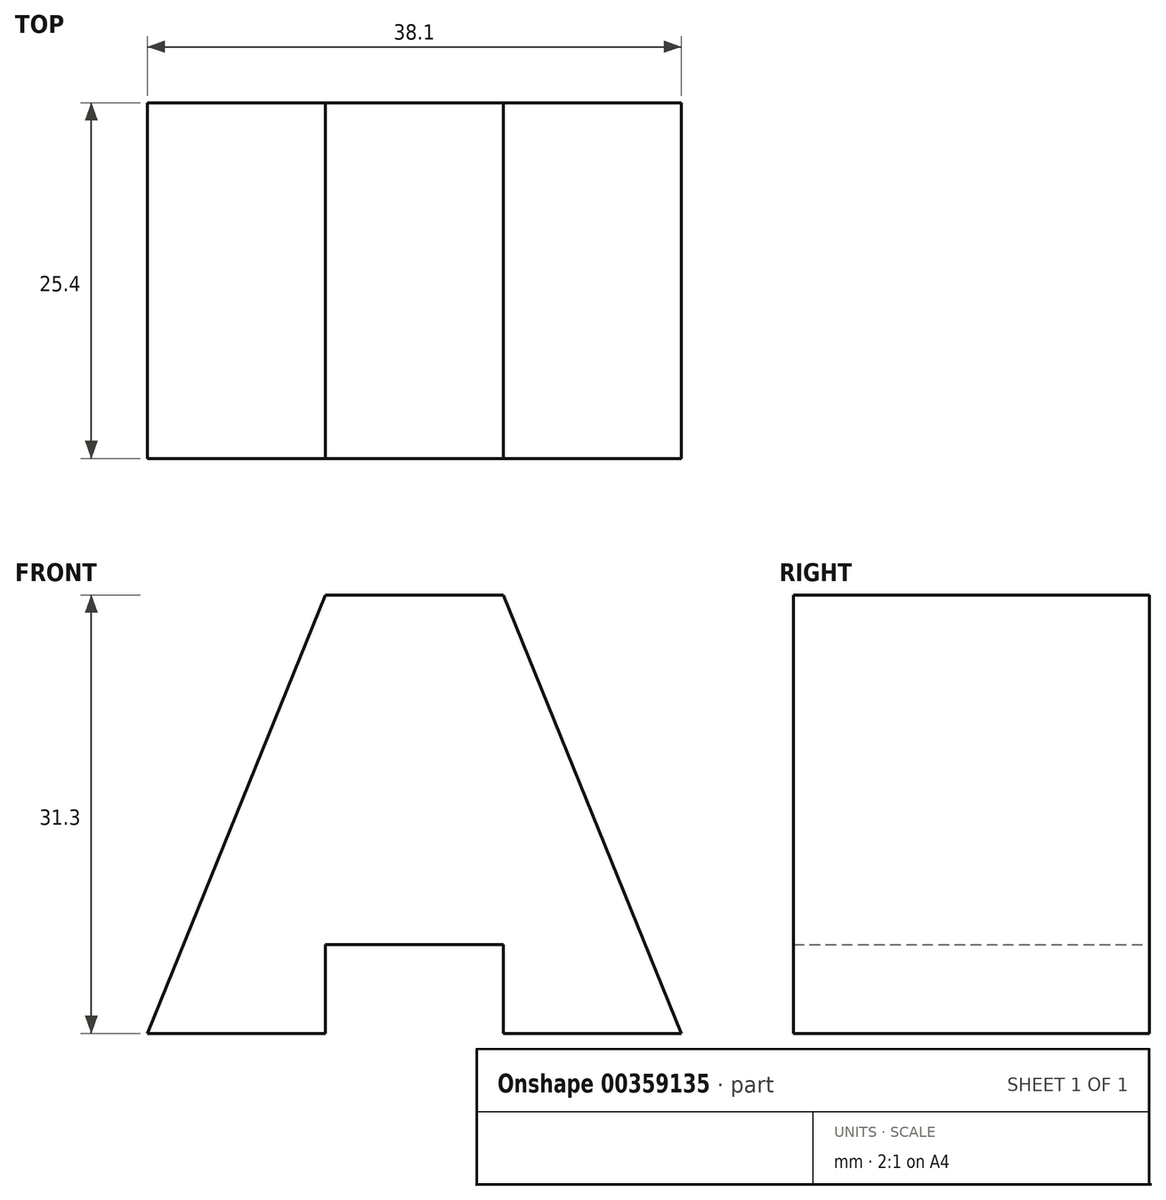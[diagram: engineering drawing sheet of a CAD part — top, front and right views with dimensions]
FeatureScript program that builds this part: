
annotation { "Feature Type Name" : "Feature", "Feature Type Description" : "" }
export const myFeature = defineFeature(function(context is Context, id is Id, definition is map)
    precondition{}
    {
        {
            var Q0;
            Q0=qCreatedBy(makeId("Front.planeOp"),FACE);
            var sketch = newSketch(context, id + "F0", { "sketchPlane" : qUnion([Q0])});
            skLineSegment(sketch, "E0", {"start": v(-42.1, -8.53) * mm, "end": v(-29.4, -8.53) * mm});
            skLineSegment(sketch, "E1", {"start": v(-29.4, -8.53) * mm, "end": v(-29.4, -2.18) * mm});
            skLineSegment(sketch, "E2", {"start": v(-29.4, -2.18) * mm, "end": v(-16.7, -2.18) * mm});
            skLineSegment(sketch, "E3", {"start": v(-16.7, -2.18) * mm, "end": v(-16.7, -8.53) * mm});
            skLineSegment(sketch, "E4", {"start": v(-16.7, -8.53) * mm, "end": v(-4, -8.53) * mm});
            skLineSegment(sketch, "E5", {"start": v(-4, -8.53) * mm, "end": v(-16.7, 22.77) * mm});
            skLineSegment(sketch, "E6", {"start": v(-16.7, 22.77) * mm, "end": v(-29.4, 22.77) * mm});
            skLineSegment(sketch, "E7", {"start": v(-29.4, 22.77) * mm, "end": v(-42.1, -8.53) * mm});
            skSolve(sketch);
        }
        {
            var Q0;
            Q0 = qSketchRegion(id + "F0", true);
            extrude(context, id + "F1", {"entities" : qUnion([Q0]), "depth" : 25.4 * mm});
        }
    });
